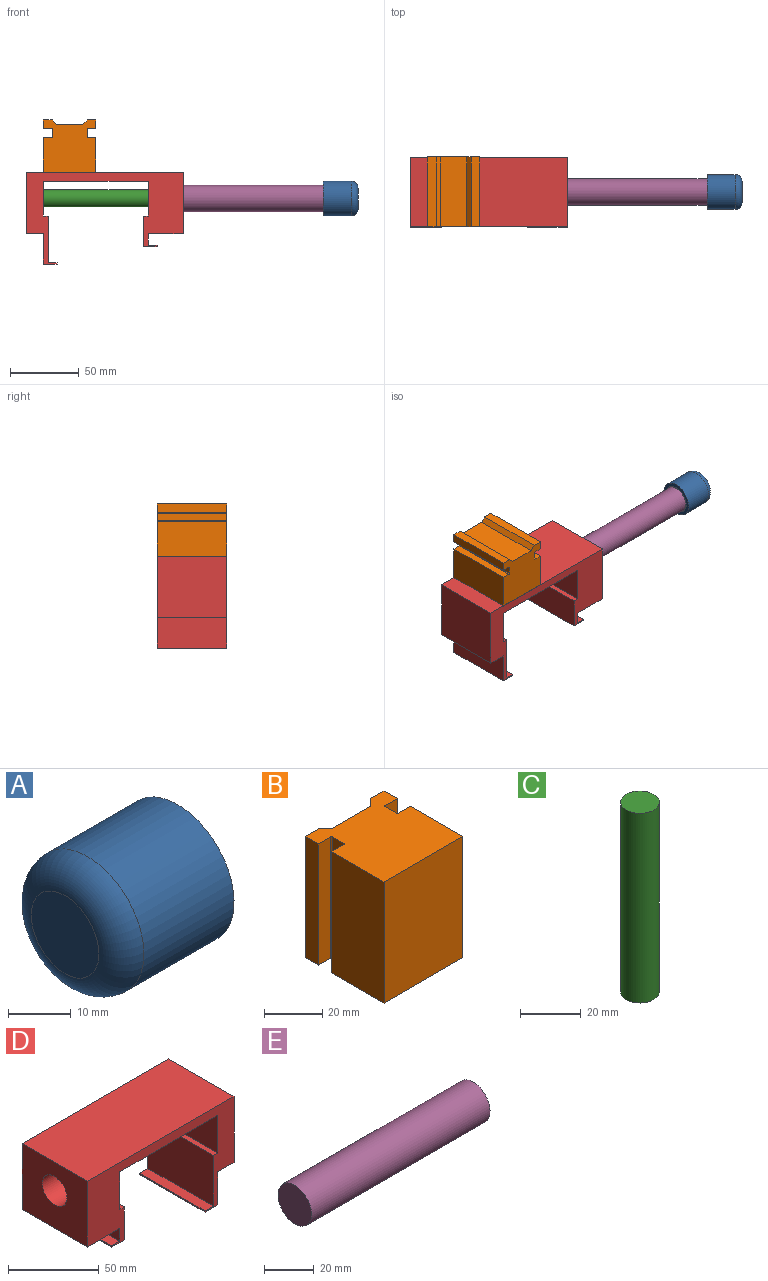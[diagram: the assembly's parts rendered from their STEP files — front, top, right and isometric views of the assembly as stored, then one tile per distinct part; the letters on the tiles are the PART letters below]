
ASSEMBLY  parts=5 mates=4
PART A: 6 faces, bbox 25.4x27.5x27.5 mm
  f0: cylinder r=12.7mm len=25.4mm, axis (-1,0,0), area 1621.5mm2, adj f1,f5
  f1: plane 25.4x25.4mm, normal (1,0,0), area 182.4mm2, adj f0,f3
  f2: plane 15.24x15.24mm, normal (-1,0,0), area 182.4mm2, adj f5
  f3: cylinder r=10.16mm len=22.86mm, axis (-1,0,0), area 1459.3mm2, adj f1,f4
  f4: plane 20.32x20.32mm, normal (1,0,0), area 324.3mm2, adj f3
  f5: torus R=7.62mm, axis (1,0,0), area 544.2mm2, adj f0,f2
PART B: 22 faces, bbox 38.1x38.1x50.8 mm
  f0: plane 50.8x38.1mm, normal (0,-1,0), area 1935.5mm2, adj f1,f15,f16,f17
  f1: plane 50.8x25.4mm, normal (1,0,0), area 1290.3mm2, adj f0,f2,f16,f17
  f2: plane 50.8x5.84mm, normal (0,1,0), area 296.8mm2, adj f1,f16,f17,f18
  f3: plane 50.8x5.33mm, normal (1,0,0), area 271mm2, adj f16,f17,f18,f19
  f4: plane 50.8x5.84mm, normal (0,-1,0), area 296.8mm2, adj f5,f16,f17,f19
  f5: plane 50.8x6.35mm, normal (1,0,0), area 322.6mm2, adj f4,f6,f16,f17
  f6: plane 50.8x6.35mm, normal (0,1,0), area 322.6mm2, adj f5,f7,f16,f17
  f7: plane 50.8x3.18mm, normal (-0.71,0.71,0), area 228.1mm2, adj f6,f8,f16,f17
  f8: plane 50.8x19.05mm, normal (0,1,0), area 967.7mm2, adj f7,f9,f16,f17
  f9: plane 50.8x3.18mm, normal (0.71,0.71,0), area 228.1mm2, adj f8,f10,f16,f17
  f10: plane 50.8x6.35mm, normal (0,1,0), area 322.6mm2, adj f9,f11,f16,f17
  f11: plane 50.8x6.35mm, normal (-1,0,0), area 322.6mm2, adj f10,f12,f16,f17
  f12: plane 50.8x5.84mm, normal (0,-1,0), area 296.8mm2, adj f11,f16,f17,f20
  f13: plane 50.8x5.33mm, normal (-1,0,0), area 271mm2, adj f16,f17,f20,f21
  f14: plane 50.8x5.84mm, normal (0,1,0), area 296.8mm2, adj f15,f16,f17,f21
  f15: plane 50.8x25.4mm, normal (-1,0,0), area 1290.3mm2, adj f0,f14,f16,f17
  f16: plane 38.1x38.1mm, normal (0,0,1), area 1300.6mm2, adj f0,f1,f2,f3,f4,f5,f6,f7
  f17: plane 38.1x38.1mm, normal (0,0,-1), area 1300.6mm2, adj f0,f1,f2,f3,f4,f5,f6,f7
  f18: cylinder r=0.51mm len=50.8mm, axis (0,0,1), area 40.5mm2, adj f2,f3,f16,f17
  f19: cylinder r=0.51mm len=50.8mm, axis (0,0,1), area 40.5mm2, adj f3,f4,f16,f17
  f20: cylinder r=0.51mm len=50.8mm, axis (0,0,1), area 40.5mm2, adj f12,f13,f16,f17
  f21: cylinder r=0.51mm len=50.8mm, axis (0,0,-1), area 40.5mm2, adj f13,f14,f16,f17
PART C: 3 faces, bbox 12.7x12.7x76.2 mm
  f0: cylinder r=6.35mm len=76.2mm, axis (0,0,-1), area 3040.2mm2, adj f1,f2
  f1: plane 12.7x12.7mm, normal (0,0,1), area 126.7mm2, adj f0
  f2: plane 12.7x12.7mm, normal (0,0,-1), area 126.7mm2, adj f0
PART D: 25 faces, bbox 114.3x50.8x66.7 mm
  f0: plane 50.8x8.67mm, normal (-1,0,0), area 440.6mm2, adj f4,f6,f10,f20
  f1: plane 50.8x34.07mm, normal (-1,0,0), area 1731mm2, adj f4,f6,f13,f15
  f2: plane 50.8x25.4mm, normal (-1,0,0), area 1163.6mm2, adj f3,f4,f6,f13,f22
  f3: plane 76.2x50.8mm, normal (0,0,-1), area 3871mm2, adj f2,f4,f6,f9
  f4: plane 114.3x66.68mm, normal (0,-1,0), area 2389.3mm2, adj f0,f1,f2,f3,f5,f7,f8,f9
  f5: plane 50.8x44.45mm, normal (1,0,0), area 2258.1mm2, adj f4,f6,f8,f11
  f6: plane 114.3x66.68mm, normal (0,1,0), area 2389.3mm2, adj f0,f1,f2,f3,f5,f7,f8,f9
  f7: plane 50.8x44.45mm, normal (-1,0,0), area 1973mm2, adj f4,f6,f8,f10,f24
  f8: plane 114.3x50.8mm, normal (0,0,1), area 5806.4mm2, adj f4,f5,f6,f7
  f9: plane 50.8x25.4mm, normal (1,0,0), area 1005.3mm2, adj f3,f4,f6,f17,f24
  f10: plane 50.8x25.4mm, normal (0,0,-1), area 1290.3mm2, adj f0,f4,f6,f7
  f11: plane 50.8x12.7mm, normal (0,0,-1), area 645.2mm2, adj f4,f5,f6,f14
  f12: plane 50.8x9.87mm, normal (0,0,-1), area 501.3mm2, adj f4,f6,f14,f16
  f13: plane 50.8x3.52mm, normal (0,0,1), area 178.7mm2, adj f1,f2,f4,f6
  f14: plane 50.8x22.23mm, normal (1,0,0), area 1129mm2, adj f4,f6,f11,f12
  f15: plane 50.8x6.35mm, normal (0,0,1), area 322.6mm2, adj f1,f4,f6,f16
  f16: plane 50.8x0.85mm, normal (-1,0,0), area 43.2mm2, adj f4,f6,f12,f15
  f17: plane 50.8x3.52mm, normal (0,0,1), area 178.7mm2, adj f4,f6,f9,f19
  f18: plane 50.8x9.87mm, normal (0,0,-1), area 501.3mm2, adj f4,f6,f19,f21
  f19: plane 50.8x22.23mm, normal (1,0,0), area 1129mm2, adj f4,f6,f17,f18
  f20: plane 50.8x6.35mm, normal (0,0,1), area 322.6mm2, adj f0,f4,f6,f21
  f21: plane 50.8x0.85mm, normal (-1,0,0), area 43.2mm2, adj f4,f6,f18,f20
  f22: cylinder r=6.35mm len=12.7mm, axis (-1,0,0), area 253.4mm2, adj f2,f23
  f23: plane 12.7x12.7mm, normal (-1,0,0), area 126.7mm2, adj f22
  f24: cylinder r=9.53mm len=25.4mm, axis (1,0,0), area 1520.1mm2, adj f7,f9
PART E: 3 faces, bbox 101.6x19.1x19.1 mm
  f0: cylinder r=9.53mm len=101.6mm, axis (-1,0,0), area 6080.5mm2, adj f1,f2
  f1: plane 19.05x19.05mm, normal (1,0,0), area 285mm2, adj f0
  f2: plane 19.05x19.05mm, normal (-1,0,0), area 285mm2, adj f0
PLACE A rot(axis=(0,1,0),180deg) t=(165.5,-108.88,-12.05)mm
PLACE B rot(axis=(1,0,0),90deg) t=(-44.05,-83.48,26.05)mm
PLACE C rot(axis=(0,-1,0),90deg) t=(13.1,-108.88,-12.05)mm
PLACE D rot(axis=(0,0,-1),180deg) t=(-18.65,-108.88,0.65)mm
PLACE E t=(38.5,-108.88,-12.05)mm
MATE fastened C.f0 <-> D.f22  axis (-1,0,0) through (-63.1,-108.88,-12.05)mm
MATE fastened B.f0 <-> D.f8  axis (0,0,-1) through (-44.05,-134.28,7)mm
MATE fastened E.f0 <-> D.f24  axis (-1,0,0) through (38.5,-108.88,-12.05)mm
MATE fastened A.f0 <-> E.f0  axis (1,0,0) through (140.1,-108.88,-12.05)mm
